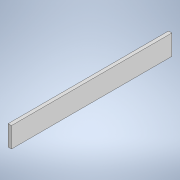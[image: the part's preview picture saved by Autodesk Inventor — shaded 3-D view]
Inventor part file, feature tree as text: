
AUTODESK INVENTOR PART (.ipt)
format: ipt  version: 2020 (Build 240168000, 168)  size: 91,648 bytes
history: native  units: mm
features: extrude x1, sketch x1
ambient origin geometry x8: Origin, YZ Plane, XZ Plane, XY Plane, X Axis, Y Axis, Z Axis, Center Point
bodies: Solid1 (feature_tree)
feature tree (2):
  extrude  "Extrusion1"  Depth=150.0mm
  sketch  "Sketch1"  dims[d0=25.0mm d1=150.0mm d2=1187.0mm d3=0.0mm]
